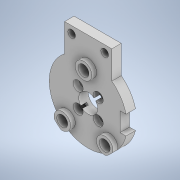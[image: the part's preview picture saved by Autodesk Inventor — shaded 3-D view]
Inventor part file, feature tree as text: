
AUTODESK INVENTOR PART (.ipt)
format: ipt  version: 2021 (Build 250183000, 183)  size: 211,456 bytes
history: native  units: mm
features: extrude x3, sketch x3, plane x1
ambient origin geometry x8: Origin, YZ Plane, XZ Plane, XY Plane, X Axis, Y Axis, Z Axis, Center Point
bodies: Solid1 (feature_tree)
feature tree (7):
  extrude  "Extrusion1"  Depth=8.5mm
  extrude  "Extrusion2"  Depth=4.25mm
  extrude  "Extrusion3"  Depth=20.0mm
  plane  "Work Plane1"
  sketch  "Sketch1"  dims[d0=33.0mm d1=8.5mm]
  sketch  "Sketch2"  dims[d2=8.5mm d3=4.25mm]
  sketch  "Sketch3"  dims[d4=4.25mm d5=2.4mm d6=8.0mm d7=13.0mm d8=4.6mm d9=10.0mm d10=9.0mm d11=9.0mm d12=4.0mm d13=0.0mm d15=2.0mm d16=0.0mm d17=3.0mm d18=8.0mm d19=4.2mm d20=2.5mm d21=0.0mm d22=1.745329mm d27=25.0mm d28=20.0mm d29=7.0mm d30=3.2mm d31=14.0mm d32=7.0mm d33=3.0mm]
